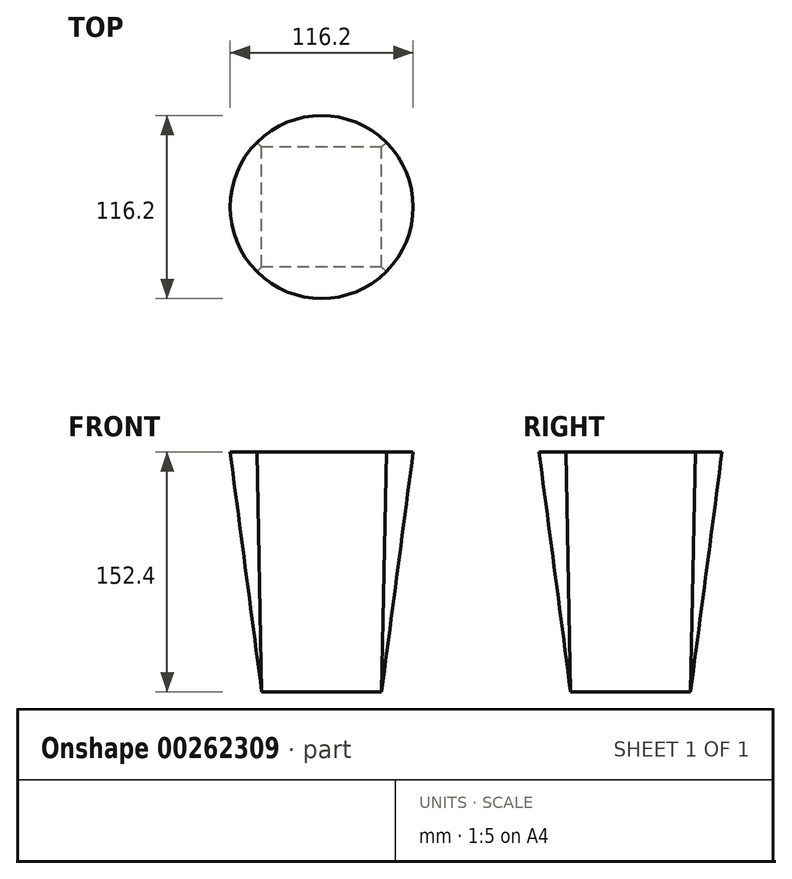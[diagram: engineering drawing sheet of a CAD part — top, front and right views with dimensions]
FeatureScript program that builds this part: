
annotation { "Feature Type Name" : "Feature", "Feature Type Description" : "" }
export const myFeature = defineFeature(function(context is Context, id is Id, definition is map)
    precondition{}
    {
        {
            var Q0;
            Q0=qCreatedBy(makeId("Top.planeOp"),FACE);
            var sketch = newSketch(context, id + "F0", { "sketchPlane" : qUnion([Q0])});
            skLineSegment(sketch, "E0.bottom", {"start": v(38.1, -38.1) * mm, "end": v(-38.1, -38.1) * mm});
            skLineSegment(sketch, "E0.top", {"start": v(38.1, 38.1) * mm, "end": v(-38.1, 38.1) * mm});
            skLineSegment(sketch, "E0.left", {"start": v(38.1, -38.1) * mm, "end": v(38.1, 38.1) * mm});
            skLineSegment(sketch, "E0.right", {"start": v(-38.1, -38.1) * mm, "end": v(-38.1, 38.1) * mm});
            skPoint(sketch, "E0.middle", {"position": v(0, 0) * mm});
            skSolve(sketch);
        }
        {
            var Q0;
            Q0=qCreatedBy(makeId("Top.planeOp"),FACE);
            cPlane(context, id + "F1", {"entities" : qUnion([Q0]), "cplaneType" : CPlaneType.OFFSET, "offset" : 152.4 * mm, "width" : 152.4 * mm, "height" : 152.4 * mm});
        }
        {
            var Q0;
            Q0=qCreatedBy(id+"F1.planeOp",FACE);
            var sketch = newSketch(context, id + "F2", { "sketchPlane" : qUnion([Q0])});
            skCircle(sketch, "E1", {"center": v(0, 0) * mm, "radius": 58.1 * mm});
            skSolve(sketch);
        }
        {
            var Q0;
            Q0=makeQuery(id+"F0.imprint","IMPRINT",FACE,{"disambiguationData":[TD([[makeQuery(id+"F0.imprint","IMPRINT",EDGE,{"derivedFrom":sQuery(id+"F0.wireOp",EDGE,"E0.bottom")}),-1.0]])]});
            var Q1;
            Q1=makeQuery(id+"F2.imprint","IMPRINT",FACE,{"disambiguationData":[TD([[makeQuery(id+"F2.imprint","IMPRINT",EDGE,{"derivedFrom":sQuery(id+"F2.wireOp",EDGE,"E1")}),1.0]])]});
            loft(context, id + "F3", {"sheetProfilesArray" : [{ "sheetProfileEntities" : qUnion([Q0]) }, { "sheetProfileEntities" : qUnion([Q1]) }]});
        }
    });
